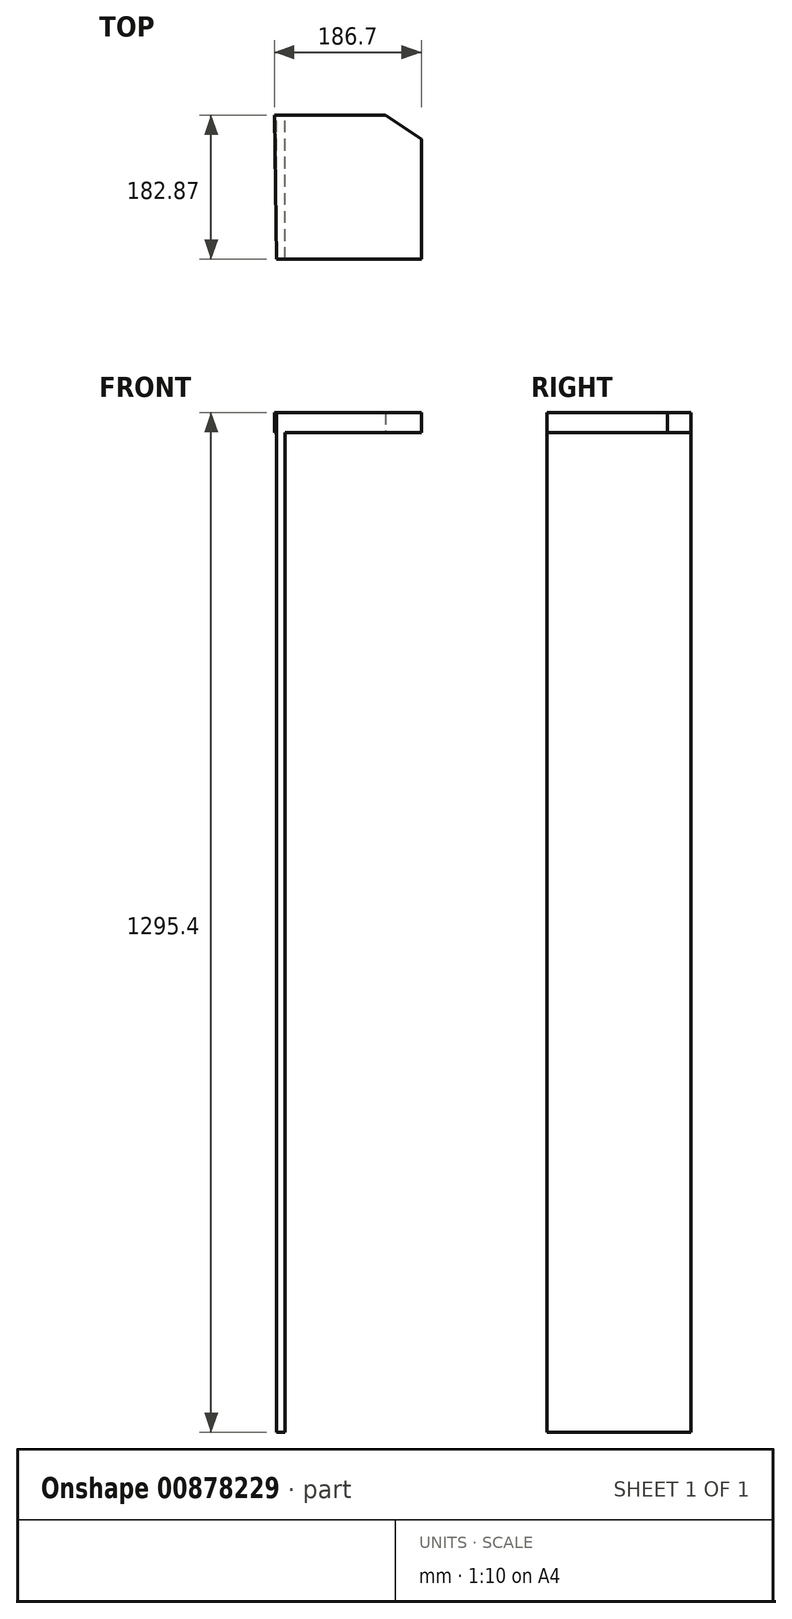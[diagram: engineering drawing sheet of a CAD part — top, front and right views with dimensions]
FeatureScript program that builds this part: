
annotation { "Feature Type Name" : "Feature", "Feature Type Description" : "" }
export const myFeature = defineFeature(function(context is Context, id is Id, definition is map)
    precondition{}
    {
        {
            var Q0;
            Q0=qCreatedBy(makeId("Top.planeOp"),FACE);
            var sketch = newSketch(context, id + "F0", { "sketchPlane" : qUnion([Q0])});
            skLineSegment(sketch, "E0", {"start": v(-91.25, -91.98) * mm, "end": v(92.87, -91.98) * mm});
            skLineSegment(sketch, "E1", {"start": v(92.87, -91.98) * mm, "end": v(92.87, 60.57) * mm});
            skLineSegment(sketch, "E2", {"start": v(-93.83, 90.9) * mm, "end": v(-91.25, -91.98) * mm});
            skLineSegment(sketch, "E3", {"start": v(-93.83, 90.9) * mm, "end": v(47.3, 90.9) * mm});
            skLineSegment(sketch, "E4", {"start": v(92.87, 60.57) * mm, "end": v(47.3, 90.9) * mm});
            skLineSegment(sketch, "E5", {"start": v(-77.01, -74.91) * mm, "end": v(77.33, -74.91) * mm});
            skLineSegment(sketch, "E6", {"start": v(77.33, -74.91) * mm, "end": v(77.33, 29.88) * mm});
            skPoint(sketch, "E7.endSnap0", {"position": v(70.09, 75.73) * mm});
            skLineSegment(sketch, "E8", {"start": v(29.39, 75.73) * mm, "end": v(-77.33, 75.73) * mm});
            skLineSegment(sketch, "E9", {"start": v(-77.33, 75.73) * mm, "end": v(-77.01, -74.91) * mm});
            skLineSegment(sketch, "E10", {"start": v(29.39, 75.73) * mm, "end": v(29.39, 90.9) * mm});
            skLineSegment(sketch, "E11", {"start": v(0, 10.32) * mm, "end": v(0, 10.32) * mm});
            skPoint(sketch, "E12.start.orphan", {"position": v(-10.68, 28.42) * mm});
            skPoint(sketch, "E13.end.orphan", {"position": v(-5.34, 25.95) * mm});
            skPoint(sketch, "E14.end.orphan", {"position": v(0, 12.98) * mm});
            skPoint(sketch, "E14.start.orphan", {"position": v(0, 23.48) * mm});
            skLineSegment(sketch, "E15", {"start": v(77.33, 29.88) * mm, "end": v(92.87, 29.88) * mm});
            skPoint(sketch, "E7.end.orphan", {"position": v(44.89, 75.73) * mm});
            skSolve(sketch);
        }
        {
            var Q0;
            Q0 = qSketchRegion(id + "F0", true);
            var Q1;
            {var subQ0=sQuery(id+"F0.wireOp",EDGE,"E4");Q1=makeQuery(id+"F0.imprint","IMPRINT",FACE,{"disambiguationData":[TD([[makeQuery(id+"F0.imprint","IMPRINT",EDGE,{"derivedFrom":subQ0}),1.0]])]});}
            extrude(context, id + "F1", {"entities" : qUnion([Q0, Q1]), "depth" : 25.4 * mm, "offsetDistance" : 25.4 * mm});
        }
        {
            var Q0;
            Q0=makeQuery(id+"F1.opExtrude","CAP_FACE",FACE,{"disambiguationData":[OSD([sQuery(id+"F0.wireOp",EDGE,"E0"),sQuery(id+"F0.wireOp",EDGE,"E1"),sQuery(id+"F0.wireOp",EDGE,"E2"),sQuery(id+"F0.wireOp",EDGE,"E3"),sQuery(id+"F0.wireOp",EDGE,"E4")])],"isStart":true});
            var sketch = newSketch(context, id + "F2", { "sketchPlane" : qUnion([Q0])});
            skLineSegment(sketch, "E16.bottom", {"start": v(-91.25, 91.98) * mm, "end": v(-80.15, 91.98) * mm});
            skLineSegment(sketch, "E16.top", {"start": v(-91.25, -90.9) * mm, "end": v(-80.15, -90.9) * mm});
            skLineSegment(sketch, "E16.left", {"start": v(-91.25, 91.98) * mm, "end": v(-91.25, -90.9) * mm});
            skLineSegment(sketch, "E16.right", {"start": v(-80.15, 91.98) * mm, "end": v(-80.15, -90.9) * mm});
            skSolve(sketch);
        }
        {
            var Q0;
            Q0=makeQuery(id+"F2.imprint","IMPRINT",FACE,{"disambiguationData":[TD([[makeQuery(id+"F2.imprint","IMPRINT",EDGE,{"derivedFrom":sQuery(id+"F2.wireOp",EDGE,"E16.bottom")}),-1.0]])]});
            extrude(context, id + "F3", {"entities" : qUnion([Q0]), "operationType" : NewBodyOperationType.ADD, "depth" : 1270 * mm, "offsetDistance" : 25.4 * mm});
        }
    });
